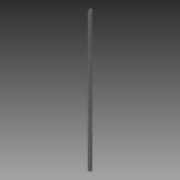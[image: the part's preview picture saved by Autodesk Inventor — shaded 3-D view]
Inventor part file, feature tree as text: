
AUTODESK INVENTOR PART (.ipt)
format: ipt  version: 2015 SP1 (Build 190203100, 203)  size: 95,744 bytes
history: native  units: mm
features: extrude x3, sketch x3
ambient origin geometry x8: Origin, YZ Plane, XZ Plane, XY Plane, X Axis, Y Axis, Z Axis, Center Point
bodies: Solid1 (feature_tree)
feature tree (6):
  extrude  "Extrusion1"  Depth=50.0mm
  extrude  "Extrusion2"  Depth=3.0mm
  extrude  "Extrusion3"  Depth=10.0mm
  sketch  "Sketch1"  dims[d0=50.0mm d1=50.0mm]
  sketch  "Sketch2"  dims[d2=3.0mm d3=3.0mm]
  sketch  "Sketch3"  dims[d4=2905.0mm d5=0.0mm d6=8.37758mm d7=2100.0mm d8=0.0mm d9=20.0mm d10=750.0mm d11=10.0mm d12=0.0mm]
